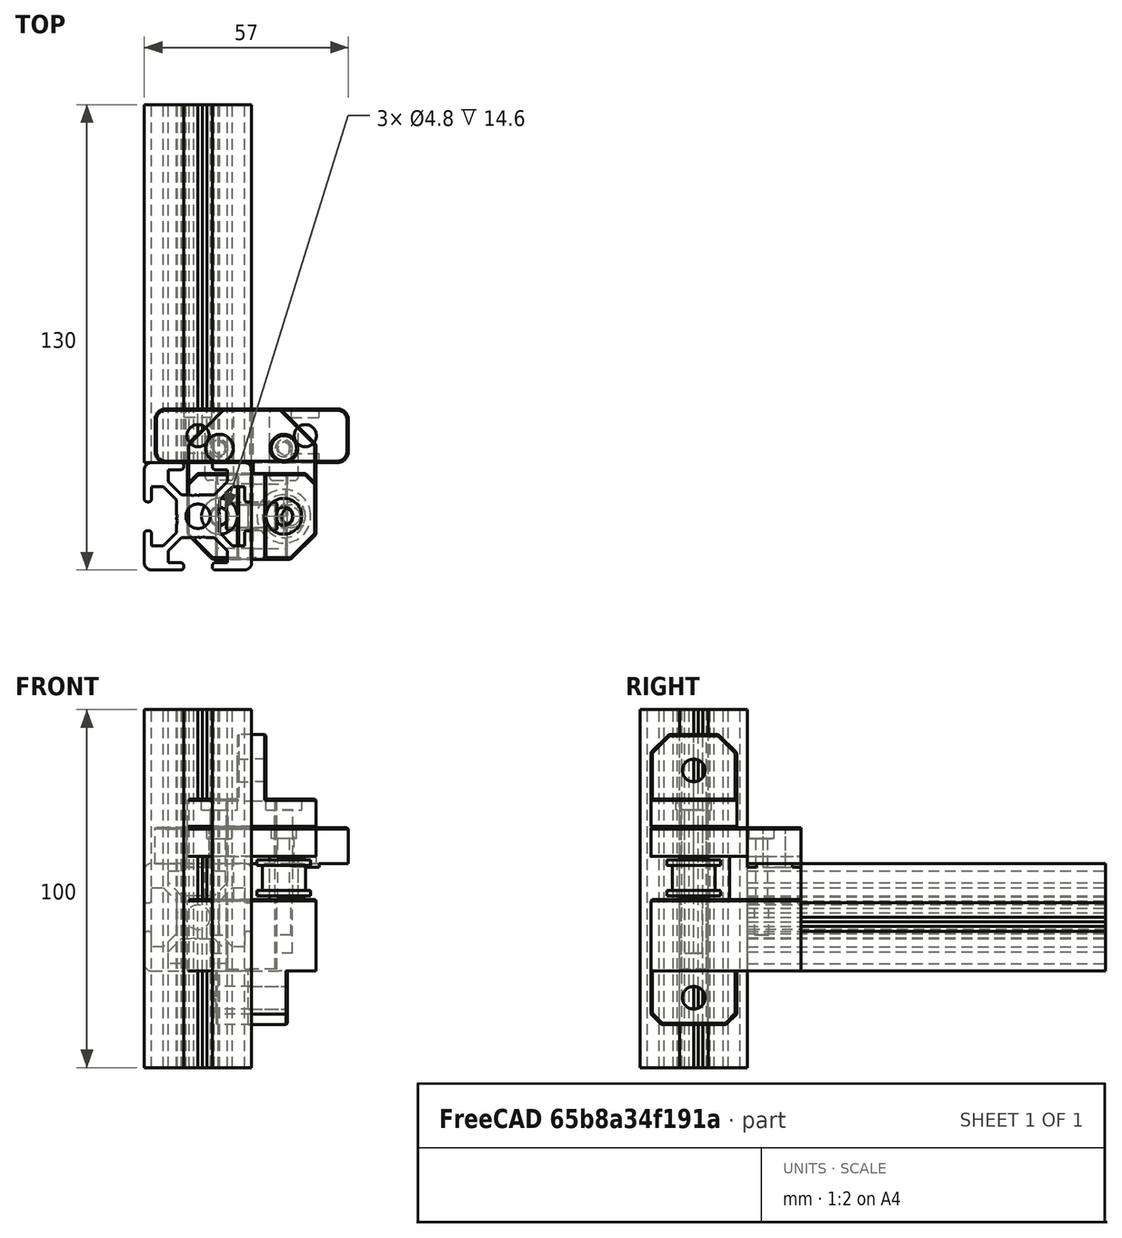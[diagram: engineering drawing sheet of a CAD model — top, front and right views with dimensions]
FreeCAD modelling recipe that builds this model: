
FCSTD DOCUMENT  (FreeCAD 0.19R24291 (Git))
Label: right-idler
License: Other
LicenseURL: GPL3
objects: Part::Box×12, Part::Feature×11, Part::Chamfer×11, Part::Cut×9, Part::Cylinder×7, Part::Fillet×5, Part::MultiFuse×3, Part::Refine×1
note: 59 computed .brp shape members not serialized (recipe doc carries the construction recipe); baked Part::Feature solids carry a one-line shape summary decoded from their .brp

FEATURE [Part::Feature] Extrude001003002002002002  label="Extrude001003002002004"
  Placement = pos=(-15,30,15) rot=(-1,0,0;1.5708rad)
  shape: bbox 30 x 100 x 30 mm, 95 faces (baked)
FEATURE [Part::Feature] Extrude001003002002002001  label="Extrude001003002002003"
  Placement = pos=(-15,15,-27) rot=(0,0,1;0rad)
  shape: bbox 30 x 30 x 100 mm, 95 faces (baked)
FEATURE [Part::Feature] Cut001  label="smooth-idler-6mm"
  Placement = pos=(9,15,21) rot=(0,0,-1;1.5708rad)
  shape: bbox 15 x 15 x 10 mm, 8 faces (baked)
FEATURE [Part::Cylinder] Cylinder001
  Angle = 360
  AttacherType = Attacher::AttachEngine3D
  Height = 35
  Placement = pos=(9,15,5) rot=(0,0,1;0rad)
  Radius = 2.525
FEATURE [Part::Box] Box006  label="Cube006"
  AttacherType = Attacher::AttachEngine3D
  Height = 15
  Length = 10
  Placement = pos=(0,3,-15) rot=(0,0,1;0rad)
  Width = 24
FEATURE [Part::Box] Box007  label="Cube007"
  AttacherType = Attacher::AttachEngine3D
  Height = 20
  Length = 7
  Placement = pos=(-7,11.1,0) rot=(0,0,1;0rad)
  Width = 7.8
FEATURE [Part::Box] Box008  label="Cube008"
  AttacherType = Attacher::AttachEngine3D
  Height = 20
  Length = 18
  Placement = pos=(0,3,0) rot=(0,0,1;0rad)
  Width = 42
FEATURE [Part::Box] Box009  label="Cube009"
  AttacherType = Attacher::AttachEngine3D
  Height = 8
  Length = 7
  Placement = pos=(-7,11.1,32) rot=(0,0,1;0rad)
  Width = 7.8
FEATURE [Part::Box] Box010  label="Cube010"
  AttacherType = Attacher::AttachEngine3D
  Height = 8
  Length = 18
  Placement = pos=(0,3,32) rot=(0,0,1;0rad)
  Width = 42
FEATURE [Part::Box] Box011  label="Cube011"
  AttacherType = Attacher::AttachEngine3D
  Height = 10
  Length = 27
  Placement = pos=(-27,30,30) rot=(0,0,1;0rad)
  Width = 15
FEATURE [Part::Cylinder] Cylinder003
  Angle = 360
  AttacherType = Attacher::AttachEngine3D
  Height = 30
  Placement = pos=(9,34,10) rot=(0,0,1;0rad)
  Radius = 2
FEATURE [Part::Chamfer] Chamfer004
  Base = -> Box006
  Edges = 2 edges r=3: [Edge9,Edge11]
FEATURE [Part::Chamfer] Chamfer005
  Base = -> Box007
  Edges = 2 edges r=0.4: [Edge1,Edge3]
FEATURE [Part::Box] Box013  label="Cube013"
  AttacherType = Attacher::AttachEngine3D
  Height = 1
  Length = 7.8
  Placement = pos=(-18.9,30,29) rot=(0,0,1;0rad)
  Width = 15
FEATURE [Part::Chamfer] Chamfer006
  Base = -> Box009
  Edges = 2 edges r=0.4: [Edge1,Edge3]
FEATURE [Part::Cylinder] Cylinder004
  Angle = 360
  AttacherType = Attacher::AttachEngine3D
  Height = 35
  Placement = pos=(9,15,5) rot=(0,0,1;0rad)
  Radius = 2.4
FEATURE [Part::Box] Box015  label="Cube015"
  AttacherType = Attacher::AttachEngine3D
  Height = 12
  Length = 8
  Placement = pos=(7,25,20) rot=(0,0,1;0rad)
  Width = 20
FEATURE [Part::Chamfer] Chamfer007
  Base = -> Box015
  Edges = 1 edges r=5: [Edge7]
FEATURE [Part::Fillet] Fillet001
  Base = -> Chamfer007
  Edges = 4 edges r=1: [Edge2,Edge3,Edge12,Edge15]
  Placement = pos=(-2,0,0) rot=(0,0,1;0rad)
FEATURE [Part::Cylinder] Cylinder005
  Angle = 360
  AttacherType = Attacher::AttachEngine3D
  Height = 31
  Placement = pos=(9,34,19) rot=(0,0,1;0rad)
  Radius = 1.65
FEATURE [Part::Cylinder] Cylinder006
  Angle = 360
  AttacherType = Attacher::AttachEngine3D
  Height = 10
  Placement = pos=(9,34,37) rot=(0,0,1;0rad)
  Radius = 3.5
FEATURE [Part::Cylinder] Cylinder008
  Angle = 360
  AttacherType = Attacher::AttachEngine3D
  Height = 14
  Placement = pos=(-2,15,-7.5) rot=(0,1,0;1.5708rad)
  Radius = 3.15
FEATURE [Part::Cylinder] Cylinder009
  Angle = 360
  AttacherType = Attacher::AttachEngine3D
  Height = 19
  Placement = pos=(-15,37.5,25) rot=(0,0,1;0rad)
  Radius = 3.1
FEATURE [Part::Feature] Cut002002002001  label="idler-washer001"
  Placement = pos=(11,15,20) rot=(0,0,1;0rad)
  shape: bbox 8 x 8 x 0.85 mm, 4 faces (baked)
FEATURE [Part::Feature] Cut002002002002  label="idler-washer002"
  Placement = pos=(11,15,32) rot=(0,1,0;3.14159rad)
  shape: bbox 8 x 8 x 0.85 mm, 4 faces (baked)
FEATURE [Part::Box] Box  label="Cube"
  AttacherType = Attacher::AttachEngine3D
  Height = 15
  Length = 1
  Placement = pos=(-1,11.1,-15) rot=(0,0,1;0rad)
  Width = 7.8
FEATURE [Part::Chamfer] Chamfer
  Base = -> Box008
  Edges = 1 edges r=7: [Edge5]
FEATURE [Part::Chamfer] Chamfer008
  Base = -> Box010
  Edges = 1 edges r=7: [Edge5]
FEATURE [Part::Chamfer] Chamfer009
  Base = -> Chamfer008
  Edges = 1 edges r=10: [Edge3]
FEATURE [Part::Chamfer] Chamfer010
  Base = -> Chamfer
  Edges = 1 edges r=10: [Edge3]
FEATURE [Part::Fillet] Fillet
  Base = -> Fillet001
  Edges = 1 edges r=1: [Edge24]
FEATURE [Part::Fillet] Fillet002
  Base = -> Chamfer010
  Edges = 4 edges r=1: [Edge2,Edge3,Edge11,Edge13]
FEATURE [Part::Chamfer] Chamfer011
  Base = -> Chamfer004
  Edges = 5 edges r=0.4: [Edge7,Edge11,Edge15,Edge16,Edge18]
FEATURE [Part::MultiFuse] Fusion
  Shapes = -> [Fillet002,Chamfer005,Chamfer011,Box]
FEATURE [Part::Cut] Cut
  Base = -> Fusion
  Tool = -> Cylinder008
FEATURE [Part::Fillet] Fillet003
  Base = -> Chamfer009
  Edges = 4 edges r=1: [Edge2,Edge3,Edge11,Edge13]
FEATURE [Part::Fillet] Fillet004
  Base = -> Box011
  Edges = 2 edges r=3: [Edge1,Edge3]
FEATURE [Part::MultiFuse] Fusion009
  Shapes = -> [Cylinder005,Cylinder006]
FEATURE [Part::Cut] Cut002002002008
  Base = -> Cut
  Tool = -> Cylinder003
FEATURE [Part::Cut] Cut002002002009
  Base = -> Cut002002002008
  Tool = -> Cylinder004
FEATURE [Part::MultiFuse] Fusion010
  Shapes = -> [Fillet004,Box013,Fillet,Chamfer006,Fillet003]
FEATURE [Part::Cut] Cut002002002009002
  Base = -> Fusion010
  Tool = -> Cylinder009
FEATURE [Part::Cut] Cut002002002009003
  Base = -> Cut002002002009002
  Tool = -> Cylinder001
FEATURE [Part::Cut] Cut002002002009004
  Base = -> Cut002002002009003
  Tool = -> Fusion009
FEATURE [Part::Feature] Cut002002002009004001  label="Cut002002002009005"
  shape: bbox 45 x 42 x 20 mm, 41 faces (baked)
FEATURE [Part::Chamfer] Chamfer012  label="top-exp"
  Base = -> Cut002002002009004001
  Edges = 21 edges r=0.4: [Edge11,Edge17,Edge20,Edge32,Edge33,Edge34,Edge35,Edge36,Edge37,Edge38,Edge39,Edge40,Edge41,Edge42,Edge43,Edge44,Edge45,Edge46,Edge47,Edge48,Edge49]
FEATURE [Part::Feature] Cut002002002007004004001001  label="top-support002"
  shape: bbox 25 x 24 x 26 mm, 66 faces (baked)
FEATURE [Part::Box] Box016  label="Cube016"
  AttacherType = Attacher::AttachEngine3D
  Height = 17
  Length = 10
  Placement = pos=(-10,10,-16.5) rot=(0,0,1;0rad)
  Width = 10
FEATURE [Part::Box] Box017  label="Cube017"
  AttacherType = Attacher::AttachEngine3D
  Height = 19
  Length = 10
  Placement = pos=(-10,10,47.5) rot=(0,0,1;0rad)
  Width = 10
FEATURE [Part::Box] Box018  label="Cube018"
  AttacherType = Attacher::AttachEngine3D
  Height = 10
  Length = 10
  Placement = pos=(-20,32.5,20) rot=(0,0,1;0rad)
  Width = 10
FEATURE [Part::Cut] Cut002002002007004004001003  label="top-support-trim"
  Base = -> Cut002002002007004004001001
  Tool = -> Box017
FEATURE [Part::Cut] Cut002002002007004004001004  label="top-trim"
  Base = -> Chamfer012
  Tool = -> Box018
FEATURE [Part::Feature] Part__Mirroring003  label="top-support-trim002 (Mirror #1)001"
  shape: bbox 25 x 24 x 26 mm, 64 faces (baked)
FEATURE [Part::Feature] Part__Mirroring002001  label="top-trim002 (Mirror #3)001"
  shape: bbox 45 x 42 x 20 mm, 66 faces (baked)
FEATURE [Part::Refine] Cut002002002009004002
  Source = -> Cut002002002009
FEATURE [Part::Chamfer] Chamfer013
  Base = -> Cut002002002009004002
  Edges = 18 edges r=0.4: [Edge13,Edge17,Edge19,Edge57,Edge60,Edge62,Edge64,Edge66,Edge68,Edge70,Edge71,Edge74,Edge78,Edge81,Edge82,Edge83,Edge84,Edge85]
FEATURE [Part::Cut] Cut002002002007004004001005
  Base = -> Chamfer013
  Tool = -> Box016
FEATURE [Part::Feature] Chamfer013001  label="bottom-exp"
  shape: bbox 25 x 42 x 35 mm, 53 faces (baked)
FEATURE [Part::Feature] Part__Mirroring002002  label="bottom-trim"
  shape: bbox 25 x 42 x 35 mm, 51 faces (baked)
